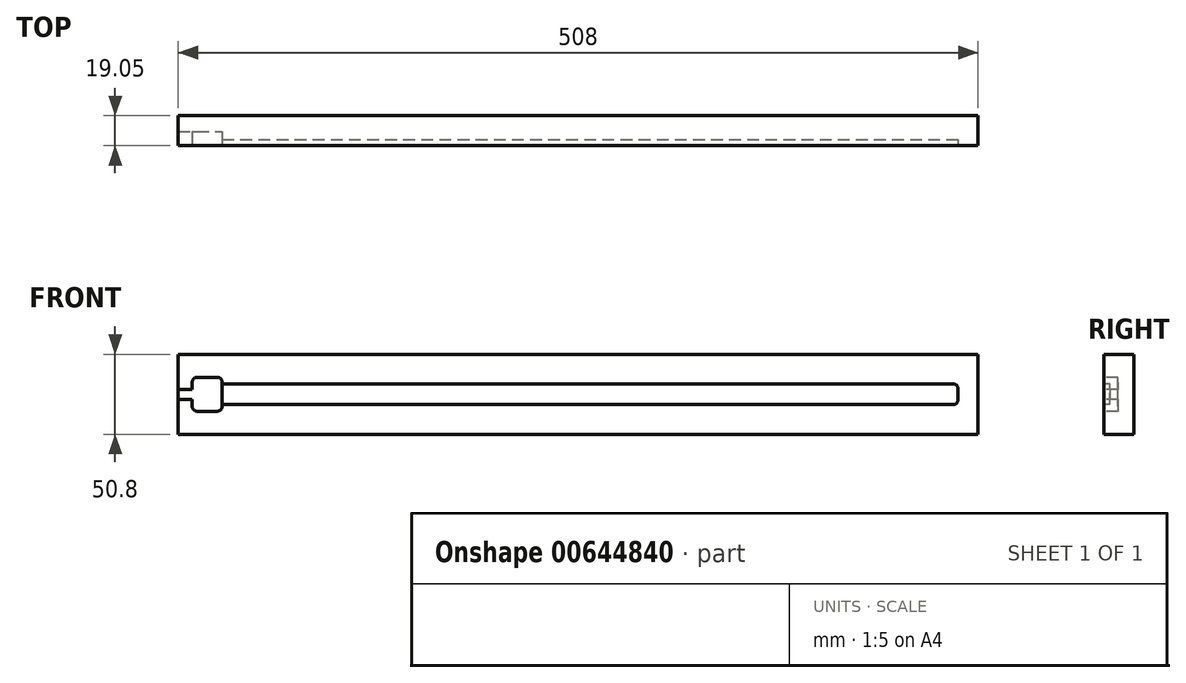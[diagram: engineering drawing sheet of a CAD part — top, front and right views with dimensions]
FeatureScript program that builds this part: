
annotation { "Feature Type Name" : "Feature", "Feature Type Description" : "" }
export const myFeature = defineFeature(function(context is Context, id is Id, definition is map)
    precondition{}
    {
        {
            var Q0;
            Q0=qCreatedBy(makeId("Front.planeOp"),FACE);
            var sketch = newSketch(context, id + "F0", { "sketchPlane" : qUnion([Q0])});
            skLineSegment(sketch, "E0.bottom", {"start": v(0, 0) * mm, "end": v(508, 0) * mm});
            skLineSegment(sketch, "E0.top", {"start": v(0, 50.8) * mm, "end": v(508, 50.8) * mm});
            skLineSegment(sketch, "E0.left", {"start": v(0, 0) * mm, "end": v(0, 50.8) * mm});
            skLineSegment(sketch, "E0.right", {"start": v(508, 0) * mm, "end": v(508, 50.8) * mm});
            skSolve(sketch);
        }
        {
            var Q0;
            Q0=makeQuery(id+"F0.imprint","IMPRINT",FACE,{"disambiguationData":[TD([[makeQuery(id+"F0.imprint","IMPRINT",EDGE,{"derivedFrom":sQuery(id+"F0.wireOp",EDGE,"E0.bottom")}),1.0]])]});
            extrude(context, id + "F1", {"entities" : qUnion([Q0]), "depth" : 19.05 * mm, "offsetDistance" : 25.4 * mm});
        }
        {
            var Q0;
            Q0=makeQuery(id+"F1.opExtrude","CAP_FACE",FACE,{"disambiguationData":[OSD([sQuery(id+"F0.wireOp",EDGE,"E0.bottom"),sQuery(id+"F0.wireOp",EDGE,"E0.top"),sQuery(id+"F0.wireOp",EDGE,"E0.left"),sQuery(id+"F0.wireOp",EDGE,"E0.right")])],"isStart":false});
            var sketch = newSketch(context, id + "F2", { "sketchPlane" : qUnion([Q0])});
            skLineSegment(sketch, "E1.bottom", {"start": v(27.94, 32) * mm, "end": v(492.13, 32) * mm});
            skLineSegment(sketch, "E1.top", {"start": v(27.94, 18.8) * mm, "end": v(492.13, 18.8) * mm});
            skLineSegment(sketch, "E1.right", {"start": v(495.3, 28.83) * mm, "end": v(495.3, 21.97) * mm});
            skLineSegment(sketch, "E2", {"start": v(27.94, 32) * mm, "end": v(27.94, 33.02) * mm});
            skLineSegment(sketch, "E3", {"start": v(24.77, 36.2) * mm, "end": v(12.07, 36.2) * mm});
            skLineSegment(sketch, "E4", {"start": v(12.07, 14.6) * mm, "end": v(24.77, 14.6) * mm});
            skLineSegment(sketch, "E5", {"start": v(27.94, 17.78) * mm, "end": v(27.94, 18.8) * mm});
            skLineSegment(sketch, "E6.trimOffspring", {"start": v(8.9, 22.23) * mm, "end": v(8.9, 17.78) * mm});
            skLineSegment(sketch, "E7", {"start": v(8.9, 33.02) * mm, "end": v(8.9, 28.58) * mm});
            skLineSegment(sketch, "E8", {"start": v(8.9, 28.58) * mm, "end": v(-2.84, 28.58) * mm});
            skLineSegment(sketch, "E9", {"start": v(-6.01, 25.4) * mm, "end": v(-6.01, 25.4) * mm});
            skLineSegment(sketch, "E10", {"start": v(-2.84, 22.23) * mm, "end": v(8.9, 22.23) * mm});
            skPoint(sketch, "E11.visualSharp", {"position": v(8.9, 36.2) * mm});
            skArc(sketch, "E11.filletArc", {"start": v(12.07, 36.2) * mm, "mid": v(9.82, 35.27) * mm, "end": v(8.9, 33.02) * mm});
            skPoint(sketch, "E12.visualSharp", {"position": v(27.94, 36.2) * mm});
            skArc(sketch, "E12.filletArc", {"start": v(27.94, 33.02) * mm, "mid": v(27.01, 35.27) * mm, "end": v(24.77, 36.2) * mm});
            skPoint(sketch, "E13.visualSharp", {"position": v(8.9, 14.6) * mm});
            skArc(sketch, "E13.filletArc", {"start": v(8.89, 17.78) * mm, "mid": v(9.82, 15.53) * mm, "end": v(12.07, 14.6) * mm});
            skPoint(sketch, "E14.visualSharp", {"position": v(27.94, 14.6) * mm});
            skArc(sketch, "E14.filletArc", {"start": v(24.77, 14.6) * mm, "mid": v(27.01, 15.53) * mm, "end": v(27.94, 17.78) * mm});
            skPoint(sketch, "E15.visualSharp", {"position": v(495.3, 18.8) * mm});
            skArc(sketch, "E15.filletArc", {"start": v(492.13, 18.8) * mm, "mid": v(494.37, 19.73) * mm, "end": v(495.3, 21.97) * mm});
            skPoint(sketch, "E16.visualSharp", {"position": v(495.3, 32) * mm});
            skArc(sketch, "E16.filletArc", {"start": v(495.3, 28.83) * mm, "mid": v(494.37, 31.07) * mm, "end": v(492.13, 32) * mm});
            skPoint(sketch, "E17.visualSharp", {"position": v(-6.01, 22.23) * mm});
            skArc(sketch, "E17.filletArc", {"start": v(-6.01, 25.4) * mm, "mid": v(-5.08, 23.15) * mm, "end": v(-2.84, 22.22) * mm});
            skPoint(sketch, "E18.visualSharp", {"position": v(-6.01, 28.58) * mm});
            skArc(sketch, "E18.filletArc", {"start": v(-2.84, 28.57) * mm, "mid": v(-5.08, 27.65) * mm, "end": v(-6.01, 25.4) * mm});
            skSolve(sketch);
        }
        {
            var Q0;
            Q0=makeQuery(id+"F2.imprint","IMPRINT",FACE,{"disambiguationData":[TD([[makeQuery(id+"F2.imprint","IMPRINT",EDGE,{"derivedFrom":sQuery(id+"F2.wireOp",EDGE,"E1.bottom")}),-1.0]])]});
            extrude(context, id + "F3", {"entities" : qUnion([Q0]), "operationType" : NewBodyOperationType.REMOVE, "oppositeDirection" : true, "depth" : 3.8 * mm, "offsetDistance" : 25.4 * mm});
        }
        {
            var Q0;
            Q0=makeQuery(id+"F1.opExtrude","CAP_FACE",FACE,{"disambiguationData":[OSD([sQuery(id+"F0.wireOp",EDGE,"E0.bottom"),sQuery(id+"F0.wireOp",EDGE,"E0.top"),sQuery(id+"F0.wireOp",EDGE,"E0.left"),sQuery(id+"F0.wireOp",EDGE,"E0.right")])],"isStart":false});
            var sketch = newSketch(context, id + "F4", { "sketchPlane" : qUnion([Q0])});
            skLineSegment(sketch, "E19", {"start": v(24.77, 14.6) * mm, "end": v(12.07, 14.6) * mm});
            skLineSegment(sketch, "E20", {"start": v(8.9, 17.78) * mm, "end": v(8.9, 22.22) * mm});
            skLineSegment(sketch, "E21", {"start": v(-6.01, 25.4) * mm, "end": v(-6.01, 25.4) * mm});
            skLineSegment(sketch, "E22", {"start": v(-2.84, 28.57) * mm, "end": v(8.9, 28.57) * mm});
            skLineSegment(sketch, "E23", {"start": v(-2.84, 22.22) * mm, "end": v(8.9, 22.22) * mm});
            skLineSegment(sketch, "E24", {"start": v(8.9, 28.57) * mm, "end": v(8.9, 33.02) * mm});
            skLineSegment(sketch, "E25", {"start": v(27.94, 17.78) * mm, "end": v(27.94, 33.02) * mm});
            skArc(sketch, "E26.filletArc", {"start": v(12.07, 36.2) * mm, "mid": v(9.82, 35.27) * mm, "end": v(8.9, 33.02) * mm});
            skArc(sketch, "E27.filletArc", {"start": v(27.94, 33.02) * mm, "mid": v(27.01, 35.27) * mm, "end": v(24.77, 36.2) * mm});
            skPoint(sketch, "E28.visualSharp", {"position": v(27.94, 14.6) * mm});
            skArc(sketch, "E28.filletArc", {"start": v(24.77, 14.6) * mm, "mid": v(27.01, 15.53) * mm, "end": v(27.94, 17.78) * mm});
            skPoint(sketch, "E29.visualSharp", {"position": v(8.9, 14.6) * mm});
            skArc(sketch, "E29.filletArc", {"start": v(8.9, 17.78) * mm, "mid": v(9.82, 15.53) * mm, "end": v(12.07, 14.6) * mm});
            skPoint(sketch, "E30.visualSharp", {"position": v(-6.01, 22.23) * mm});
            skArc(sketch, "E30.filletArc", {"start": v(-6.01, 25.4) * mm, "mid": v(-5.08, 23.15) * mm, "end": v(-2.84, 22.23) * mm});
            skPoint(sketch, "E31.visualSharp", {"position": v(-6.01, 28.57) * mm});
            skArc(sketch, "E31.filletArc", {"start": v(-2.84, 28.57) * mm, "mid": v(-5.08, 27.65) * mm, "end": v(-6.01, 25.4) * mm});
            skLineSegment(sketch, "E32", {"start": v(12.07, 36.2) * mm, "end": v(24.77, 36.2) * mm});
            skSolve(sketch);
        }
        {
            var Q0;
            Q0 = qSketchRegion(id + "F4", true);
            extrude(context, id + "F5", {"entities" : qUnion([Q0]), "operationType" : NewBodyOperationType.REMOVE, "oppositeDirection" : true, "depth" : 8.9 * mm, "offsetDistance" : 25.4 * mm});
        }
    });
